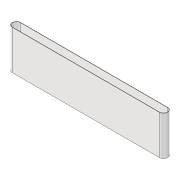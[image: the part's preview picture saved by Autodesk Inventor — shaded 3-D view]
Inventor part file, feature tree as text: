
AUTODESK INVENTOR PART (.ipt)
format: ipt  version: 2020 (Build 240168000, 168)  size: 88,064 bytes
history: native  units: mm
features: extrude x1, sketch x1
ambient origin geometry x8: Origin, YZ Plane, XZ Plane, XY Plane, X Axis, Y Axis, Z Axis, Center Point
bodies: Volumenkörper1 (feature_tree)
feature tree (2):
  extrude  "Extrusion1"  Depth=86.0mm
  sketch  "Skizze1"  dims[d0=80.0mm d1=86.0mm d2=80.0mm d3=86.0mm d4=1500.0mm d5=340.0mm d6=0.0mm]
